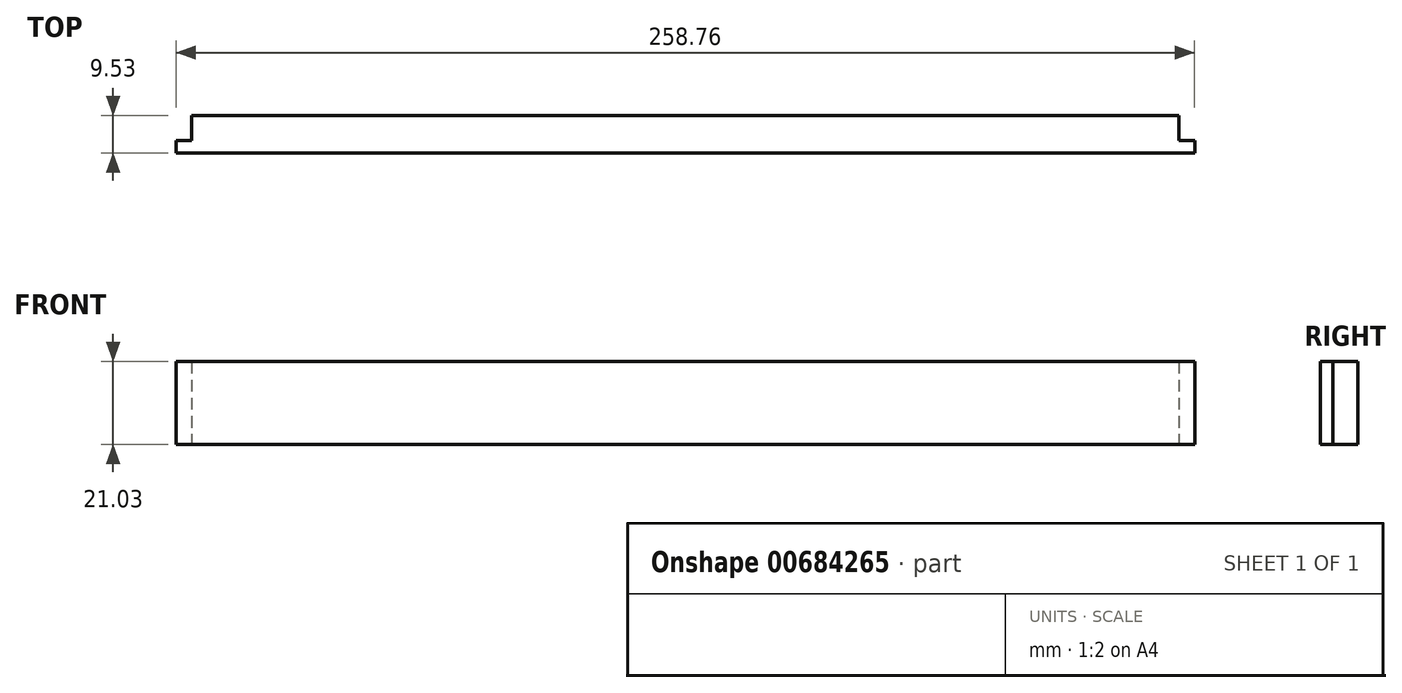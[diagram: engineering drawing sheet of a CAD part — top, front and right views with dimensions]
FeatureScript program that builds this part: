
annotation { "Feature Type Name" : "Feature", "Feature Type Description" : "" }
export const myFeature = defineFeature(function(context is Context, id is Id, definition is map)
    precondition{}
    {
        {
            var Q0;
            Q0=qCreatedBy(makeId("Top.planeOp"),FACE);
            var sketch = newSketch(context, id + "F0", { "sketchPlane" : qUnion([Q0])});
            skLineSegment(sketch, "E0.bottom", {"start": v(-125.41, 0) * mm, "end": v(125.41, 0) * mm});
            skLineSegment(sketch, "E0.top", {"start": v(-125.41, 9.53) * mm, "end": v(125.41, 9.53) * mm});
            skLineSegment(sketch, "E0.left", {"start": v(-125.41, 0) * mm, "end": v(-125.41, 9.53) * mm});
            skLineSegment(sketch, "E0.right", {"start": v(125.41, 0) * mm, "end": v(125.41, 9.53) * mm});
            skLineSegment(sketch, "E1.left", {"start": v(125.41, 9.53) * mm, "end": v(125.41, 3.17) * mm});
            skLineSegment(sketch, "E2", {"start": v(125.41, 3.17) * mm, "end": v(129.38, 3.17) * mm});
            skLineSegment(sketch, "E3", {"start": v(129.38, 3.17) * mm, "end": v(129.38, 0) * mm});
            skLineSegment(sketch, "E4", {"start": v(129.38, 0) * mm, "end": v(125.41, 0) * mm});
            skLineSegment(sketch, "E5.MirrorCS", {"start": v(-125.41, 3.17) * mm, "end": v(-129.38, 3.17) * mm});
            skLineSegment(sketch, "E6.MirrorCS", {"start": v(-129.38, 3.17) * mm, "end": v(-129.38, 0) * mm});
            skLineSegment(sketch, "E7.MirrorCS", {"start": v(-129.38, 0) * mm, "end": v(-125.41, 0) * mm});
            skSolve(sketch);
        }
        {
            var Q0;
            Q0=makeQuery(id+"F0.imprint","IMPRINT",FACE,{"disambiguationData":[TD([[makeQuery(id+"F0.imprint","IMPRINT",EDGE,{"derivedFrom":sQuery(id+"F0.wireOp",EDGE,"E0.bottom")}),1.0]])]});
            var Q1;
            {var subQ2=sQuery(id+"F0.wireOp",EDGE,"E5.MirrorCS");Q1=makeQuery(id+"F0.imprint","IMPRINT",FACE,{"disambiguationData":[TD([[makeQuery(id+"F0.imprint","IMPRINT",EDGE,{"derivedFrom":subQ2}),1.0]])]});}
            var Q2;
            Q2=makeQuery(id+"F0.imprint","IMPRINT",FACE,{"disambiguationData":[TD([[makeQuery(id+"F0.imprint","IMPRINT",EDGE,{"derivedFrom":sQuery(id+"F0.wireOp",EDGE,"E0.right")}),-1.0]])]});
            extrude(context, id + "F1", {"entities" : qUnion([Q0, Q1, Q2]), "depth" : 21.03 * mm, "offsetDistance" : 25.4 * mm});
        }
    });
